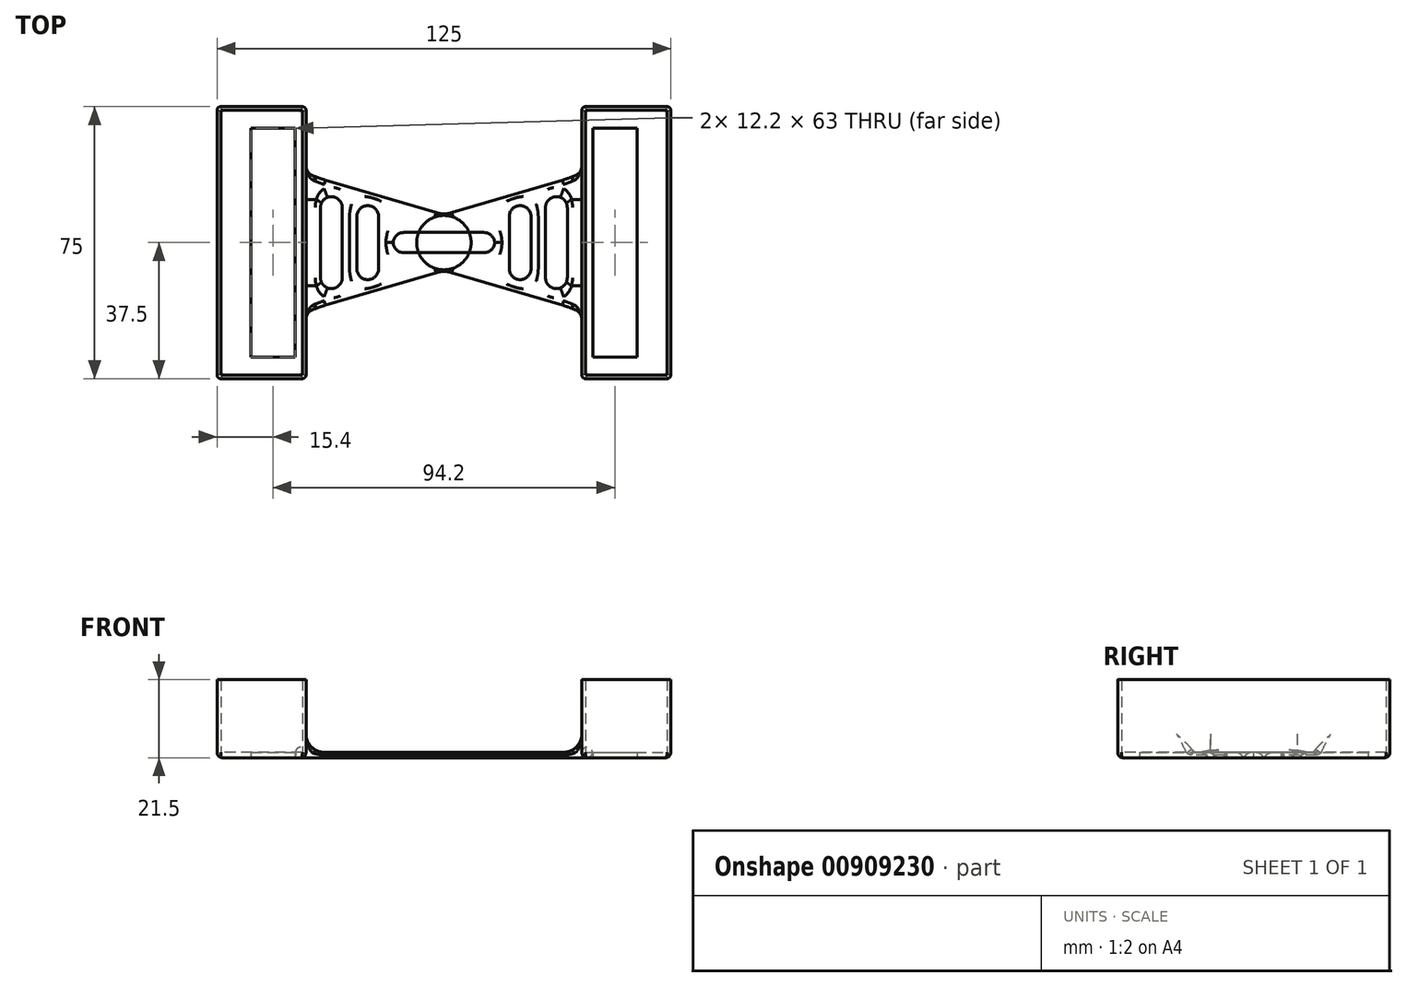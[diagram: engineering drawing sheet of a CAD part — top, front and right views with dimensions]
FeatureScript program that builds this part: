
annotation { "Feature Type Name" : "Feature", "Feature Type Description" : "" }
export const myFeature = defineFeature(function(context is Context, id is Id, definition is map)
    precondition{}
    {
        {
            var Q0;
            Q0=qCreatedBy(makeId("Top.planeOp"),FACE);
            var sketch = newSketch(context, id + "F0", { "sketchPlane" : qUnion([Q0])});
            skLineSegment(sketch, "E0", {"start": v(-62.5, 0) * mm, "end": v(62.5, 0) * mm, "construction": true});
            skLineSegment(sketch, "E1", {"start": v(-62.5, 0) * mm, "end": v(-62.5, 37.5) * mm});
            skLineSegment(sketch, "E2", {"start": v(-62.5, 0) * mm, "end": v(-62.5, -37.5) * mm});
            skLineSegment(sketch, "E3", {"start": v(62.5, 37.5) * mm, "end": v(62.5, 0) * mm});
            skLineSegment(sketch, "E4", {"start": v(62.5, 0) * mm, "end": v(62.5, -37.5) * mm});
            skLineSegment(sketch, "E5", {"start": v(-38, 37.5) * mm, "end": v(-38, -37.5) * mm});
            skLineSegment(sketch, "E6", {"start": v(38, 37.5) * mm, "end": v(38, -37.5) * mm});
            skLineSegment(sketch, "E7", {"start": v(-62.5, 37.5) * mm, "end": v(-38, 37.5) * mm});
            skLineSegment(sketch, "E8", {"start": v(-62.5, -37.5) * mm, "end": v(-38, -37.5) * mm});
            skLineSegment(sketch, "E9", {"start": v(38, -37.5) * mm, "end": v(62.5, -37.5) * mm});
            skLineSegment(sketch, "E10", {"start": v(38, 37.5) * mm, "end": v(62.5, 37.5) * mm});
            skLineSegment(sketch, "E11", {"start": v(-41, 31.5) * mm, "end": v(-41, -31.5) * mm});
            skLineSegment(sketch, "E12", {"start": v(-41, -31.5) * mm, "end": v(-53.2, -31.5) * mm});
            skLineSegment(sketch, "E13", {"start": v(-53.2, -31.5) * mm, "end": v(-53.2, 31.5) * mm});
            skLineSegment(sketch, "E14", {"start": v(-53.2, 31.5) * mm, "end": v(-41, 31.5) * mm});
            skLineSegment(sketch, "E15", {"start": v(41, 31.5) * mm, "end": v(53.2, 31.5) * mm});
            skLineSegment(sketch, "E16", {"start": v(53.2, 31.5) * mm, "end": v(53.2, -31.5) * mm});
            skLineSegment(sketch, "E17", {"start": v(53.2, -31.5) * mm, "end": v(41, -31.5) * mm});
            skLineSegment(sketch, "E18", {"start": v(41, -31.5) * mm, "end": v(41, 31.5) * mm});
            skCircle(sketch, "E19", {"center": v(0, 0) * mm, "radius": 7.5 * mm});
            skLineSegment(sketch, "E20", {"start": v(-38, 19) * mm, "end": v(0, 7.82) * mm});
            skLineSegment(sketch, "E21", {"start": v(0, 7.82) * mm, "end": v(38, 19) * mm});
            skPoint(sketch, "E22", {"position": v(-38, -19) * mm});
            skLineSegment(sketch, "E23", {"start": v(-38, -19) * mm, "end": v(0, -7.82) * mm});
            skLineSegment(sketch, "E24", {"start": v(0, -7.82) * mm, "end": v(38, -19) * mm});
            skLineSegment(sketch, "E25.bottom", {"start": v(-28, 12.67) * mm, "end": v(-34, 12.67) * mm});
            skLineSegment(sketch, "E25.top", {"start": v(-28, -12.67) * mm, "end": v(-34, -12.67) * mm});
            skLineSegment(sketch, "E25.left", {"start": v(-28, 12.67) * mm, "end": v(-28, -12.67) * mm});
            skLineSegment(sketch, "E25.right", {"start": v(-34, 12.67) * mm, "end": v(-34, -12.67) * mm});
            skPoint(sketch, "E25.middle", {"position": v(-31, 0) * mm});
            skLineSegment(sketch, "E26.bottom", {"start": v(-24, 10.2) * mm, "end": v(-18, 10.2) * mm});
            skLineSegment(sketch, "E26.top", {"start": v(-24, -10.2) * mm, "end": v(-18, -10.2) * mm});
            skLineSegment(sketch, "E26.left", {"start": v(-24, 10.2) * mm, "end": v(-24, -10.2) * mm});
            skLineSegment(sketch, "E26.right", {"start": v(-18, 10.2) * mm, "end": v(-18, -10.2) * mm});
            skPoint(sketch, "E26.middle", {"position": v(-21, 0) * mm});
            skLineSegment(sketch, "E27.bottom", {"start": v(14, 2.8) * mm, "end": v(-14, 2.8) * mm});
            skLineSegment(sketch, "E27.top", {"start": v(14, -2.8) * mm, "end": v(-14, -2.8) * mm});
            skLineSegment(sketch, "E27.left", {"start": v(14, 2.8) * mm, "end": v(14, -2.8) * mm});
            skLineSegment(sketch, "E27.right", {"start": v(-14, 2.8) * mm, "end": v(-14, -2.8) * mm});
            skLineSegment(sketch, "E28.bottom", {"start": v(18, 10.2) * mm, "end": v(24, 10.2) * mm});
            skLineSegment(sketch, "E28.top", {"start": v(18, -10.2) * mm, "end": v(24, -10.2) * mm});
            skLineSegment(sketch, "E28.left", {"start": v(18, 10.2) * mm, "end": v(18, -10.2) * mm});
            skLineSegment(sketch, "E28.right", {"start": v(24, 10.2) * mm, "end": v(24, -10.2) * mm});
            skPoint(sketch, "E28.middle", {"position": v(21, 0) * mm});
            skLineSegment(sketch, "E29.bottom", {"start": v(28, -12.67) * mm, "end": v(34, -12.67) * mm});
            skLineSegment(sketch, "E29.top", {"start": v(28, 12.67) * mm, "end": v(34, 12.67) * mm});
            skLineSegment(sketch, "E29.left", {"start": v(28, -12.67) * mm, "end": v(28, 12.67) * mm});
            skLineSegment(sketch, "E29.right", {"start": v(34, -12.67) * mm, "end": v(34, 12.67) * mm});
            skPoint(sketch, "E29.middle", {"position": v(31, 0) * mm});
            skSolve(sketch);
        }
        {
            var Q0;
            Q0 = qSketchRegion(id + "F0", true);
            var Q1;
            {var subQ0=sQuery(id+"F0.wireOp",EDGE,"E27.top");var subQ1=sQuery(id+"F0.wireOp",EDGE,"E19");var subQ2=makeQuery(id+"F0.imprint","INTERSECT",VERTEX,{"disambiguationData":[OD(0.0)],"derivedFrom":[subQ1,subQ0]});Q1=makeQuery(id+"F0.imprint","IMPRINT",FACE,{"disambiguationData":[TD([[makeQuery(id+"F0.imprint","IMPRINT",EDGE,{"disambiguationData":[TD([[subQ2,-1.0]])],"derivedFrom":subQ1}),1.0]])]});}
            var Q2;
            {var subQ0=sQuery(id+"F0.wireOp",EDGE,"E27.bottom");var subQ1=sQuery(id+"F0.wireOp",EDGE,"E19");var subQ2=makeQuery(id+"F0.imprint","INTERSECT",VERTEX,{"disambiguationData":[OD(0.0)],"derivedFrom":[subQ1,subQ0]});Q2=makeQuery(id+"F0.imprint","IMPRINT",FACE,{"disambiguationData":[TD([[makeQuery(id+"F0.imprint","IMPRINT",EDGE,{"disambiguationData":[TD([[subQ2,1.0]])],"derivedFrom":subQ1}),1.0]])]});}
            extrude(context, id + "F1", {"entities" : qUnion([Q0, Q1, Q2]), "depth" : 1.5 * mm, "offsetDistance" : 25 * mm});
        }
        {
            var Q0;
            Q0=makeQuery(id+"F1.opExtrude","CAP_FACE",FACE,{"disambiguationData":[OSD([sQuery(id+"F0.wireOp",EDGE,"E1"),sQuery(id+"F0.wireOp",EDGE,"E2"),sQuery(id+"F0.wireOp",EDGE,"E3"),sQuery(id+"F0.wireOp",EDGE,"E4"),sQuery(id+"F0.wireOp",EDGE,"E5"),sQuery(id+"F0.wireOp",EDGE,"E6"),sQuery(id+"F0.wireOp",EDGE,"E7"),sQuery(id+"F0.wireOp",EDGE,"E8"),sQuery(id+"F0.wireOp",EDGE,"E9"),sQuery(id+"F0.wireOp",EDGE,"E10"),sQuery(id+"F0.wireOp",EDGE,"E11"),sQuery(id+"F0.wireOp",EDGE,"E12"),sQuery(id+"F0.wireOp",EDGE,"E13"),sQuery(id+"F0.wireOp",EDGE,"E14"),sQuery(id+"F0.wireOp",EDGE,"E15"),sQuery(id+"F0.wireOp",EDGE,"E16"),sQuery(id+"F0.wireOp",EDGE,"E17"),sQuery(id+"F0.wireOp",EDGE,"E18"),sQuery(id+"F0.wireOp",EDGE,"E20"),sQuery(id+"F0.wireOp",EDGE,"E21"),sQuery(id+"F0.wireOp",EDGE,"E23"),sQuery(id+"F0.wireOp",EDGE,"E24"),sQuery(id+"F0.wireOp",EDGE,"E25.bottom"),sQuery(id+"F0.wireOp",EDGE,"E25.top"),sQuery(id+"F0.wireOp",EDGE,"E25.left"),sQuery(id+"F0.wireOp",EDGE,"E25.right"),sQuery(id+"F0.wireOp",EDGE,"E26.bottom"),sQuery(id+"F0.wireOp",EDGE,"E26.top"),sQuery(id+"F0.wireOp",EDGE,"E26.left"),sQuery(id+"F0.wireOp",EDGE,"E26.right"),sQuery(id+"F0.wireOp",EDGE,"E27.bottom"),sQuery(id+"F0.wireOp",EDGE,"E27.top"),sQuery(id+"F0.wireOp",EDGE,"E27.left"),sQuery(id+"F0.wireOp",EDGE,"E27.right"),sQuery(id+"F0.wireOp",EDGE,"E28.bottom"),sQuery(id+"F0.wireOp",EDGE,"E28.top"),sQuery(id+"F0.wireOp",EDGE,"E28.left"),sQuery(id+"F0.wireOp",EDGE,"E28.right"),sQuery(id+"F0.wireOp",EDGE,"E29.bottom"),sQuery(id+"F0.wireOp",EDGE,"E29.top"),sQuery(id+"F0.wireOp",EDGE,"E29.left"),sQuery(id+"F0.wireOp",EDGE,"E29.right")])],"isStart":false});
            var sketch = newSketch(context, id + "F2", { "sketchPlane" : qUnion([Q0])});
            skLineSegment(sketch, "E30.bottom", {"start": v(-62.5, 37.5) * mm, "end": v(-38, 37.5) * mm});
            skLineSegment(sketch, "E30.top", {"start": v(-62.5, -37.5) * mm, "end": v(-38, -37.5) * mm});
            skLineSegment(sketch, "E30.left", {"start": v(-62.5, 37.5) * mm, "end": v(-62.5, -37.5) * mm});
            skLineSegment(sketch, "E30.right", {"start": v(-38, 37.5) * mm, "end": v(-38, -37.5) * mm});
            skLineSegment(sketch, "E31.bottom", {"start": v(38, 37.5) * mm, "end": v(62.5, 37.5) * mm});
            skLineSegment(sketch, "E31.top", {"start": v(38, -37.5) * mm, "end": v(62.5, -37.5) * mm});
            skLineSegment(sketch, "E31.left", {"start": v(38, 37.5) * mm, "end": v(38, -37.5) * mm});
            skLineSegment(sketch, "E31.right", {"start": v(62.5, 37.5) * mm, "end": v(62.5, -37.5) * mm});
            skLineSegment(sketch, "E32.bottom", {"start": v(-39, -36.5) * mm, "end": v(-61.5, -36.5) * mm});
            skLineSegment(sketch, "E32.top", {"start": v(-39, 36.5) * mm, "end": v(-61.5, 36.5) * mm});
            skLineSegment(sketch, "E32.left", {"start": v(-39, -36.5) * mm, "end": v(-39, 36.5) * mm});
            skLineSegment(sketch, "E32.right", {"start": v(-61.5, -36.5) * mm, "end": v(-61.5, 36.5) * mm});
            skLineSegment(sketch, "E33.bottom", {"start": v(39, 36.5) * mm, "end": v(61.5, 36.5) * mm});
            skLineSegment(sketch, "E33.top", {"start": v(39, -36.5) * mm, "end": v(61.5, -36.5) * mm});
            skLineSegment(sketch, "E33.left", {"start": v(39, 36.5) * mm, "end": v(39, -36.5) * mm});
            skLineSegment(sketch, "E33.right", {"start": v(61.5, 36.5) * mm, "end": v(61.5, -36.5) * mm});
            skLineSegment(sketch, "E34", {"start": v(-61.5, -36.5) * mm, "end": v(-61.5, -37.5) * mm});
            skLineSegment(sketch, "E35", {"start": v(-39, -36.5) * mm, "end": v(-39, -37.5) * mm});
            skLineSegment(sketch, "E36", {"start": v(-61.5, 36.5) * mm, "end": v(-61.5, 37.5) * mm});
            skLineSegment(sketch, "E37", {"start": v(-39, 36.5) * mm, "end": v(-39, 37.5) * mm});
            skLineSegment(sketch, "E38", {"start": v(39, -36.5) * mm, "end": v(39, -37.5) * mm});
            skLineSegment(sketch, "E39", {"start": v(61.5, -36.5) * mm, "end": v(61.5, -37.5) * mm});
            skLineSegment(sketch, "E40", {"start": v(61.5, 36.5) * mm, "end": v(61.5, 37.5) * mm});
            skLineSegment(sketch, "E41", {"start": v(39, 36.5) * mm, "end": v(39, 37.5) * mm});
            skSolve(sketch);
        }
        {
            var Q0;
            {var subQ0=sQuery(id+"F2.wireOp",EDGE,"E30.left");Q0=makeQuery(id+"F2.imprint","IMPRINT",FACE,{"disambiguationData":[TD([[makeQuery(id+"F2.imprint","IMPRINT",EDGE,{"derivedFrom":subQ0}),-1.0]])]});}
            var Q1;
            {var subQ0=sQuery(id+"F2.wireOp",EDGE,"E31.right");Q1=makeQuery(id+"F2.imprint","IMPRINT",FACE,{"disambiguationData":[TD([[makeQuery(id+"F2.imprint","IMPRINT",EDGE,{"derivedFrom":subQ0}),-1.0]])]});}
            var Q2;
            Q2=makeQuery(id+"F2.imprint","IMPRINT",FACE,{"disambiguationData":[TD([[makeQuery(id+"F2.imprint","IMPRINT",EDGE,{"derivedFrom":sQuery(id+"F2.wireOp",EDGE,"E32.left")}),-1.0]])]});
            var Q3;
            Q3=makeQuery(id+"F2.imprint","IMPRINT",FACE,{"disambiguationData":[TD([[makeQuery(id+"F2.imprint","IMPRINT",EDGE,{"derivedFrom":sQuery(id+"F2.wireOp",EDGE,"E33.left")}),-1.0]])]});
            var Q4;
            Q4=makeQuery(id+"F2.imprint","IMPRINT",FACE,{"disambiguationData":[TD([[makeQuery(id+"F2.imprint","IMPRINT",EDGE,{"derivedFrom":sQuery(id+"F2.wireOp",EDGE,"E33.bottom")}),1.0]])]});
            var Q5;
            Q5=makeQuery(id+"F2.imprint","IMPRINT",FACE,{"disambiguationData":[TD([[makeQuery(id+"F2.imprint","IMPRINT",EDGE,{"derivedFrom":sQuery(id+"F2.wireOp",EDGE,"E33.top")}),-1.0]])]});
            var Q6;
            Q6=makeQuery(id+"F2.imprint","IMPRINT",FACE,{"disambiguationData":[TD([[makeQuery(id+"F2.imprint","IMPRINT",EDGE,{"derivedFrom":sQuery(id+"F2.wireOp",EDGE,"E32.top")}),-1.0]])]});
            var Q7;
            Q7=makeQuery(id+"F2.imprint","IMPRINT",FACE,{"disambiguationData":[TD([[makeQuery(id+"F2.imprint","IMPRINT",EDGE,{"derivedFrom":sQuery(id+"F2.wireOp",EDGE,"E32.bottom")}),1.0]])]});
            extrude(context, id + "F3", {"entities" : qUnion([Q0, Q1, Q2, Q3, Q4, Q5, Q6, Q7]), "operationType" : NewBodyOperationType.ADD, "depth" : 20 * mm, "offsetDistance" : 25 * mm});
        }
        {
            var Q0;
            Q0=makeQuery(id+"F1.opExtrude","SWEPT_EDGE",EDGE,{"disambiguationData":[OSD([sQuery(id+"F0.wireOp",EDGE,"E20"),sQuery(id+"F0.wireOp",EDGE,"E21")])]});
            var Q1;
            Q1=makeQuery(id+"F1.opExtrude","SWEPT_EDGE",EDGE,{"disambiguationData":[OSD([sQuery(id+"F0.wireOp",EDGE,"E23"),sQuery(id+"F0.wireOp",EDGE,"E24")])]});
            var Q2;
            Q2=makeQuery(id+"F1.opExtrude","SWEPT_EDGE",EDGE,{"disambiguationData":[OSD([sQuery(id+"F0.wireOp",EDGE,"E29.bottom"),sQuery(id+"F0.wireOp",EDGE,"E29.right")])]});
            var Q3;
            Q3=makeQuery(id+"F1.opExtrude","SWEPT_EDGE",EDGE,{"disambiguationData":[OSD([sQuery(id+"F0.wireOp",EDGE,"E27.top"),sQuery(id+"F0.wireOp",EDGE,"E27.left")])]});
            var Q4;
            Q4=makeQuery(id+"F1.opExtrude","SWEPT_EDGE",EDGE,{"disambiguationData":[OSD([sQuery(id+"F0.wireOp",EDGE,"E26.top"),sQuery(id+"F0.wireOp",EDGE,"E26.right")])]});
            var Q5;
            Q5=makeQuery(id+"F1.opExtrude","SWEPT_EDGE",EDGE,{"disambiguationData":[OSD([sQuery(id+"F0.wireOp",EDGE,"E25.top"),sQuery(id+"F0.wireOp",EDGE,"E25.right")])]});
            var Q6;
            Q6=makeQuery(id+"F1.opExtrude","SWEPT_EDGE",EDGE,{"disambiguationData":[OSD([sQuery(id+"F0.wireOp",EDGE,"E26.top"),sQuery(id+"F0.wireOp",EDGE,"E26.left")])]});
            var Q7;
            Q7=makeQuery(id+"F1.opExtrude","SWEPT_EDGE",EDGE,{"disambiguationData":[OSD([sQuery(id+"F0.wireOp",EDGE,"E25.top"),sQuery(id+"F0.wireOp",EDGE,"E25.left")])]});
            var Q8;
            Q8=makeQuery(id+"F1.opExtrude","SWEPT_EDGE",EDGE,{"disambiguationData":[OSD([sQuery(id+"F0.wireOp",EDGE,"E28.top"),sQuery(id+"F0.wireOp",EDGE,"E28.left")])]});
            var Q9;
            Q9=makeQuery(id+"F1.opExtrude","SWEPT_EDGE",EDGE,{"disambiguationData":[OSD([sQuery(id+"F0.wireOp",EDGE,"E26.bottom"),sQuery(id+"F0.wireOp",EDGE,"E26.right")])]});
            var Q10;
            Q10=makeQuery(id+"F1.opExtrude","SWEPT_EDGE",EDGE,{"disambiguationData":[OSD([sQuery(id+"F0.wireOp",EDGE,"E25.bottom"),sQuery(id+"F0.wireOp",EDGE,"E25.left")])]});
            var Q11;
            Q11=makeQuery(id+"F1.opExtrude","SWEPT_EDGE",EDGE,{"disambiguationData":[OSD([sQuery(id+"F0.wireOp",EDGE,"E25.bottom"),sQuery(id+"F0.wireOp",EDGE,"E25.right")])]});
            var Q12;
            Q12=makeQuery(id+"F1.opExtrude","SWEPT_EDGE",EDGE,{"disambiguationData":[OSD([sQuery(id+"F0.wireOp",EDGE,"E26.bottom"),sQuery(id+"F0.wireOp",EDGE,"E26.left")])]});
            var Q13;
            Q13=makeQuery(id+"F1.opExtrude","SWEPT_EDGE",EDGE,{"disambiguationData":[OSD([sQuery(id+"F0.wireOp",EDGE,"E27.bottom"),sQuery(id+"F0.wireOp",EDGE,"E27.right")])]});
            var Q14;
            Q14=makeQuery(id+"F1.opExtrude","SWEPT_EDGE",EDGE,{"disambiguationData":[OSD([sQuery(id+"F0.wireOp",EDGE,"E27.bottom"),sQuery(id+"F0.wireOp",EDGE,"E27.left")])]});
            var Q15;
            Q15=makeQuery(id+"F1.opExtrude","SWEPT_EDGE",EDGE,{"disambiguationData":[OSD([sQuery(id+"F0.wireOp",EDGE,"E27.top"),sQuery(id+"F0.wireOp",EDGE,"E27.right")])]});
            var Q16;
            Q16=makeQuery(id+"F1.opExtrude","SWEPT_EDGE",EDGE,{"disambiguationData":[OSD([sQuery(id+"F0.wireOp",EDGE,"E28.bottom"),sQuery(id+"F0.wireOp",EDGE,"E28.left")])]});
            var Q17;
            Q17=makeQuery(id+"F1.opExtrude","SWEPT_EDGE",EDGE,{"disambiguationData":[OSD([sQuery(id+"F0.wireOp",EDGE,"E5"),sQuery(id+"F0.wireOp",EDGE,"E20")])]});
            var Q18;
            Q18=makeQuery(id+"F1.opExtrude","SWEPT_EDGE",EDGE,{"disambiguationData":[OSD([sQuery(id+"F0.wireOp",EDGE,"E6"),sQuery(id+"F0.wireOp",EDGE,"E21")])]});
            var Q19;
            Q19=makeQuery(id+"F1.opExtrude","SWEPT_EDGE",EDGE,{"disambiguationData":[OSD([sQuery(id+"F0.wireOp",EDGE,"E6"),sQuery(id+"F0.wireOp",EDGE,"E24")])]});
            var Q20;
            Q20=makeQuery(id+"F1.opExtrude","SWEPT_EDGE",EDGE,{"disambiguationData":[OSD([sQuery(id+"F0.wireOp",EDGE,"E5"),sQuery(id+"F0.wireOp",EDGE,"E23")])]});
            var Q21;
            Q21=makeQuery(id+"F1.opExtrude","SWEPT_EDGE",EDGE,{"disambiguationData":[OSD([sQuery(id+"F0.wireOp",EDGE,"E28.top"),sQuery(id+"F0.wireOp",EDGE,"E28.right")])]});
            var Q22;
            Q22=makeQuery(id+"F1.opExtrude","SWEPT_EDGE",EDGE,{"disambiguationData":[OSD([sQuery(id+"F0.wireOp",EDGE,"E28.bottom"),sQuery(id+"F0.wireOp",EDGE,"E28.right")])]});
            var Q23;
            Q23=makeQuery(id+"F1.opExtrude","SWEPT_EDGE",EDGE,{"disambiguationData":[OSD([sQuery(id+"F0.wireOp",EDGE,"E29.top"),sQuery(id+"F0.wireOp",EDGE,"E29.right")])]});
            var Q24;
            Q24=makeQuery(id+"F1.opExtrude","SWEPT_EDGE",EDGE,{"disambiguationData":[OSD([sQuery(id+"F0.wireOp",EDGE,"E29.bottom"),sQuery(id+"F0.wireOp",EDGE,"E29.left")])]});
            var Q25;
            Q25=makeQuery(id+"F1.opExtrude","SWEPT_EDGE",EDGE,{"disambiguationData":[OSD([sQuery(id+"F0.wireOp",EDGE,"E29.top"),sQuery(id+"F0.wireOp",EDGE,"E29.left")])]});
            fillet(context, id + "F4", {"entities" : qUnion([Q0, Q1, Q2, Q3, Q4, Q5, Q6, Q7, Q8, Q9, Q10, Q11, Q12, Q13, Q14, Q15, Q16, Q17, Q18, Q19, Q20, Q21, Q22, Q23, Q24, Q25]), "radius" : 3 * mm, "tangentPropagation" : true, "allowEdgeOverflow" : false});
        }
        {
            var Q0;
            Q0=makeQuery(id+"F3.boolean.opBoolean","MERGE",EDGE,{"derivedFrom":[makeQuery(id+"F1.opExtrude","SWEPT_EDGE",EDGE,{"disambiguationData":[OSD([sQuery(id+"F0.wireOp",EDGE,"E3"),sQuery(id+"F0.wireOp",EDGE,"E10")])]}),makeQuery(id+"F3.opExtrude","SWEPT_EDGE",EDGE,{"disambiguationData":[OSD([sQuery(id+"F2.wireOp",EDGE,"E31.bottom"),sQuery(id+"F2.wireOp",EDGE,"E31.right")])]})]});
            var Q1;
            Q1=makeQuery(id+"F3.boolean.opBoolean","MERGE",EDGE,{"derivedFrom":[makeQuery(id+"F1.opExtrude","SWEPT_EDGE",EDGE,{"disambiguationData":[OSD([sQuery(id+"F0.wireOp",EDGE,"E6"),sQuery(id+"F0.wireOp",EDGE,"E10")])]}),makeQuery(id+"F3.opExtrude","SWEPT_EDGE",EDGE,{"disambiguationData":[OSD([sQuery(id+"F2.wireOp",EDGE,"E31.bottom"),sQuery(id+"F2.wireOp",EDGE,"E31.left")])]})]});
            var Q2;
            Q2=makeQuery(id+"F3.boolean.opBoolean","MERGE",EDGE,{"derivedFrom":[makeQuery(id+"F1.opExtrude","SWEPT_EDGE",EDGE,{"disambiguationData":[OSD([sQuery(id+"F0.wireOp",EDGE,"E1"),sQuery(id+"F0.wireOp",EDGE,"E7")])]}),makeQuery(id+"F3.opExtrude","SWEPT_EDGE",EDGE,{"disambiguationData":[OSD([sQuery(id+"F2.wireOp",EDGE,"E30.bottom"),sQuery(id+"F2.wireOp",EDGE,"E30.left")])]})]});
            var Q3;
            Q3=makeQuery(id+"F3.boolean.opBoolean","MERGE",EDGE,{"derivedFrom":[makeQuery(id+"F1.opExtrude","SWEPT_EDGE",EDGE,{"disambiguationData":[OSD([sQuery(id+"F0.wireOp",EDGE,"E5"),sQuery(id+"F0.wireOp",EDGE,"E7")])]}),makeQuery(id+"F3.opExtrude","SWEPT_EDGE",EDGE,{"disambiguationData":[OSD([sQuery(id+"F2.wireOp",EDGE,"E30.bottom"),sQuery(id+"F2.wireOp",EDGE,"E30.right")])]})]});
            var Q4;
            Q4=makeQuery(id+"F3.boolean.opBoolean","MERGE",EDGE,{"derivedFrom":[makeQuery(id+"F1.opExtrude","SWEPT_EDGE",EDGE,{"disambiguationData":[OSD([sQuery(id+"F0.wireOp",EDGE,"E4"),sQuery(id+"F0.wireOp",EDGE,"E9")])]}),makeQuery(id+"F3.opExtrude","SWEPT_EDGE",EDGE,{"disambiguationData":[OSD([sQuery(id+"F2.wireOp",EDGE,"E31.top"),sQuery(id+"F2.wireOp",EDGE,"E31.right")])]})]});
            var Q5;
            Q5=makeQuery(id+"F3.boolean.opBoolean","MERGE",EDGE,{"derivedFrom":[makeQuery(id+"F1.opExtrude","SWEPT_EDGE",EDGE,{"disambiguationData":[OSD([sQuery(id+"F0.wireOp",EDGE,"E6"),sQuery(id+"F0.wireOp",EDGE,"E9")])]}),makeQuery(id+"F3.opExtrude","SWEPT_EDGE",EDGE,{"disambiguationData":[OSD([sQuery(id+"F2.wireOp",EDGE,"E31.top"),sQuery(id+"F2.wireOp",EDGE,"E31.left")])]})]});
            var Q6;
            Q6=makeQuery(id+"F3.boolean.opBoolean","MERGE",EDGE,{"derivedFrom":[makeQuery(id+"F1.opExtrude","SWEPT_EDGE",EDGE,{"disambiguationData":[OSD([sQuery(id+"F0.wireOp",EDGE,"E2"),sQuery(id+"F0.wireOp",EDGE,"E8")])]}),makeQuery(id+"F3.opExtrude","SWEPT_EDGE",EDGE,{"disambiguationData":[OSD([sQuery(id+"F2.wireOp",EDGE,"E30.top"),sQuery(id+"F2.wireOp",EDGE,"E30.left")])]})]});
            var Q7;
            Q7=makeQuery(id+"F3.boolean.opBoolean","MERGE",EDGE,{"derivedFrom":[makeQuery(id+"F1.opExtrude","SWEPT_EDGE",EDGE,{"disambiguationData":[OSD([sQuery(id+"F0.wireOp",EDGE,"E5"),sQuery(id+"F0.wireOp",EDGE,"E8")])]}),makeQuery(id+"F3.opExtrude","SWEPT_EDGE",EDGE,{"disambiguationData":[OSD([sQuery(id+"F2.wireOp",EDGE,"E30.top"),sQuery(id+"F2.wireOp",EDGE,"E30.right")])]})]});
            fillet(context, id + "F5", {"entities" : qUnion([Q0, Q1, Q2, Q3, Q4, Q5, Q6, Q7]), "radius" : 1 * mm, "tangentPropagation" : true, "allowEdgeOverflow" : false});
        }
        {
            var Q0;
            Q0=makeQuery(id+"F3.opExtrude","CAP_EDGE",EDGE,{"disambiguationData":[OSD([sQuery(id+"F2.wireOp",EDGE,"E30.right")])],"isStart":true});
            var Q1;
            Q1=makeQuery(id+"F3.opExtrude","CAP_EDGE",EDGE,{"disambiguationData":[OSD([sQuery(id+"F2.wireOp",EDGE,"E31.left")])],"isStart":true});
            fillet(context, id + "F6", {"entities" : qUnion([Q0, Q1]), "radius" : 5 * mm, "tangentPropagation" : true, "allowEdgeOverflow" : false});
        }
        {
            var Q0;
            Q0=makeQuery(id+"F4.opFillet","BLEND_FACE",FACE,{"disambiguationData":[OSD([sQuery(id+"F0.wireOp",EDGE,"E20"),sQuery(id+"F0.wireOp",EDGE,"E21")])]});
            var Q1;
            Q1=makeQuery(id+"F4.opFillet","BLEND_FACE",FACE,{"disambiguationData":[OSD([sQuery(id+"F0.wireOp",EDGE,"E23"),sQuery(id+"F0.wireOp",EDGE,"E24")])]});
            fillet(context, id + "F7", {"entities" : qUnion([Q0, Q1]), "radius" : 1.45 * mm, "tangentPropagation" : true, "allowEdgeOverflow" : false});
        }
        {
            var Q0;
            Q0=makeQuery(id+"F6.opFillet","BLEND_EDGE",EDGE,{"blendedFrom":[makeQuery(id+"F3.opExtrude","CAP_EDGE",EDGE,{"disambiguationData":[OSD([sQuery(id+"F2.wireOp",EDGE,"E31.left")])],"isStart":true}),makeQuery(id+"F1.opExtrude","SWEPT_FACE",FACE,{"disambiguationData":[OSD([sQuery(id+"F0.wireOp",EDGE,"E29.right")])]})],"blendedInto":[makeQuery(id+"F1.opExtrude","SWEPT_FACE",FACE,{"disambiguationData":[OSD([sQuery(id+"F0.wireOp",EDGE,"E29.right")])]})]});
            var Q1;
            Q1=makeQuery(id+"F1.opExtrude","CAP_EDGE",EDGE,{"disambiguationData":[OSD([sQuery(id+"F0.wireOp",EDGE,"E28.right")])],"isStart":false});
            var Q2;
            Q2=makeQuery(id+"F1.opExtrude","CAP_EDGE",EDGE,{"disambiguationData":[OSD([sQuery(id+"F0.wireOp",EDGE,"E27.top")])],"isStart":false});
            var Q3;
            Q3=makeQuery(id+"F1.opExtrude","CAP_EDGE",EDGE,{"disambiguationData":[OSD([sQuery(id+"F0.wireOp",EDGE,"E26.right")])],"isStart":false});
            var Q4;
            Q4=makeQuery(id+"F6.opFillet","BLEND_EDGE",EDGE,{"blendedFrom":[makeQuery(id+"F3.opExtrude","CAP_EDGE",EDGE,{"disambiguationData":[OSD([sQuery(id+"F2.wireOp",EDGE,"E30.right")])],"isStart":true}),makeQuery(id+"F1.opExtrude","SWEPT_FACE",FACE,{"disambiguationData":[OSD([sQuery(id+"F0.wireOp",EDGE,"E25.right")])]})],"blendedInto":[makeQuery(id+"F1.opExtrude","SWEPT_FACE",FACE,{"disambiguationData":[OSD([sQuery(id+"F0.wireOp",EDGE,"E25.right")])]})]});
            var Q5;
            Q5=makeQuery(id+"F1.opExtrude","CAP_EDGE",EDGE,{"disambiguationData":[OSD([sQuery(id+"F0.wireOp",EDGE,"E27.bottom")])],"isStart":false});
            fillet(context, id + "F8", {"entities" : qUnion([Q0, Q1, Q2, Q3, Q4, Q5]), "radius" : 3 * mm, "tangentPropagation" : true, "allowEdgeOverflow" : false});
        }
    });
